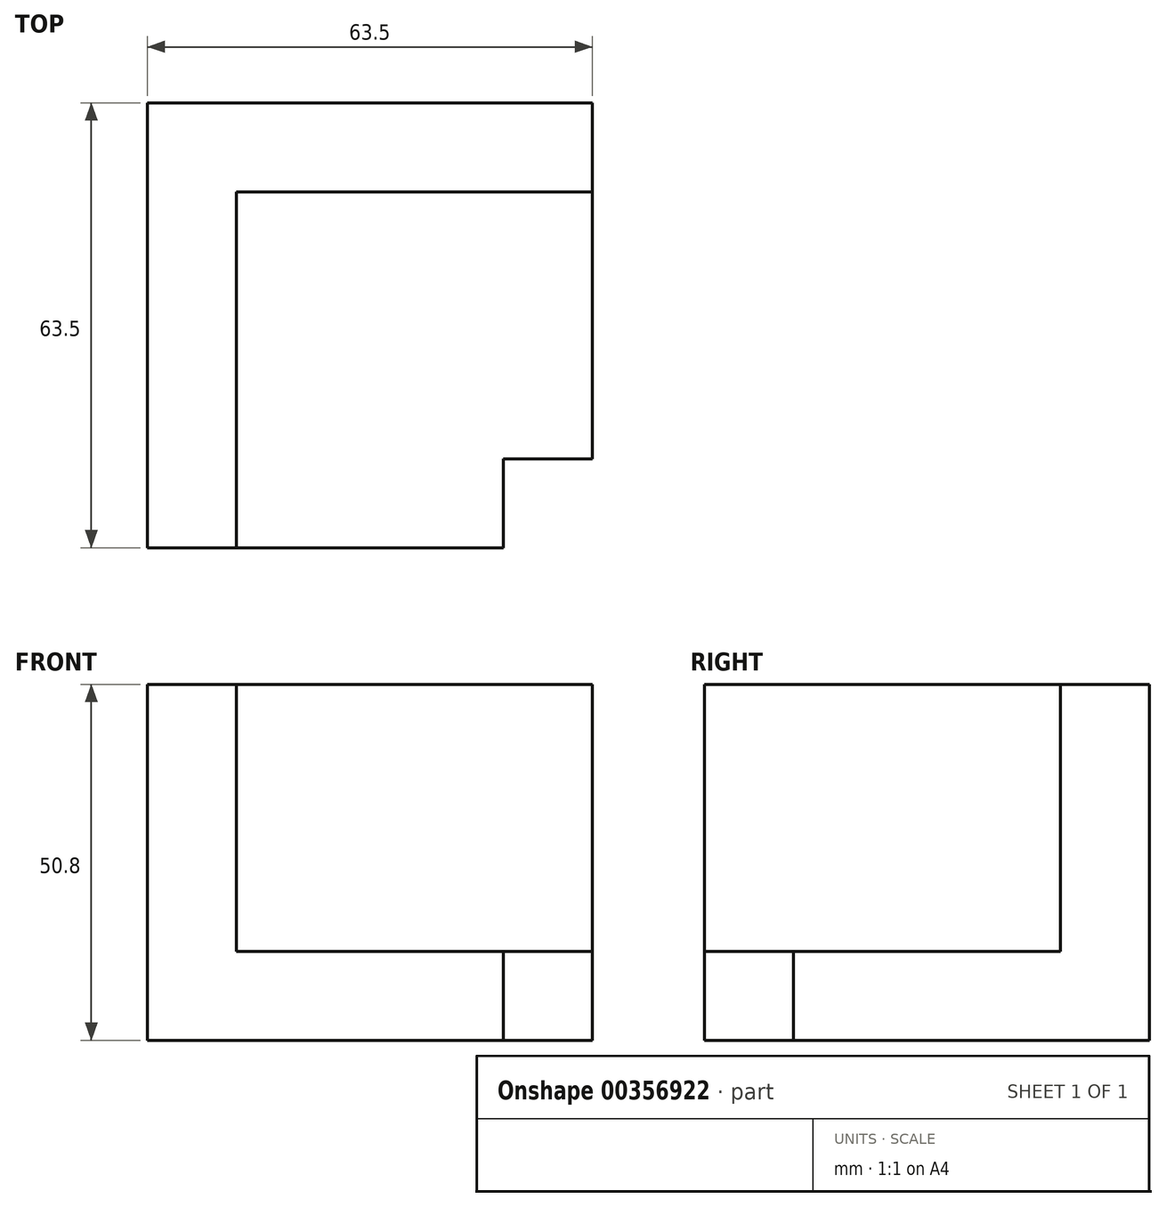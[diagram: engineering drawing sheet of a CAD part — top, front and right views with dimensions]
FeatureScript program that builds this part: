
annotation { "Feature Type Name" : "Feature", "Feature Type Description" : "" }
export const myFeature = defineFeature(function(context is Context, id is Id, definition is map)
    precondition{}
    {
        {
            var Q0;
            Q0=qCreatedBy(makeId("Front.planeOp"),FACE);
            var sketch = newSketch(context, id + "F0", { "sketchPlane" : qUnion([Q0])});
            skLineSegment(sketch, "E0.bottom", {"start": v(0, 0) * mm, "end": v(12.7, 0) * mm});
            skLineSegment(sketch, "E0.top", {"start": v(0, -50.8) * mm, "end": v(12.7, -50.8) * mm});
            skLineSegment(sketch, "E0.left", {"start": v(0, 0) * mm, "end": v(0, -50.8) * mm});
            skLineSegment(sketch, "E0.right", {"start": v(12.7, 0) * mm, "end": v(12.7, -50.8) * mm});
            skSolve(sketch);
        }
        {
            var Q0;
            Q0 = qSketchRegion(id + "F0", true);
            var Q1;
            Q1=makeQuery(id+"F0.imprint","IMPRINT",FACE,{"disambiguationData":[TD([[makeQuery(id+"F0.imprint","IMPRINT",EDGE,{"derivedFrom":sQuery(id+"F0.wireOp",EDGE,"E0.bottom")}),-1.0]])]});
            extrude(context, id + "F1", {"entities" : qUnion([Q0, Q1]), "depth" : 63.5 * mm});
        }
        {
            var Q0;
            Q0=makeQuery(id+"F1.opExtrude","SWEPT_FACE",FACE,{"disambiguationData":[OSD([sQuery(id+"F0.wireOp",EDGE,"E0.right")])]});
            var sketch = newSketch(context, id + "F2", { "sketchPlane" : qUnion([Q0])});
            skLineSegment(sketch, "E1.bottom", {"start": v(0, 0) * mm, "end": v(-12.7, 0) * mm});
            skLineSegment(sketch, "E1.top", {"start": v(0, -50.8) * mm, "end": v(-12.7, -50.8) * mm});
            skLineSegment(sketch, "E1.left", {"start": v(0, 0) * mm, "end": v(0, -50.8) * mm});
            skLineSegment(sketch, "E1.right", {"start": v(-12.7, 0) * mm, "end": v(-12.7, -50.8) * mm});
            skSolve(sketch);
        }
        {
            var Q0;
            Q0 = qSketchRegion(id + "F2", true);
            extrude(context, id + "F3", {"entities" : qUnion([Q0]), "operationType" : NewBodyOperationType.ADD, "depth" : 50.8 * mm});
        }
        {
            var Q0;
            Q0=makeQuery(id+"F1.opExtrude","SWEPT_FACE",FACE,{"disambiguationData":[OSD([sQuery(id+"F0.wireOp",EDGE,"E0.right")])]});
            var sketch = newSketch(context, id + "F4", { "sketchPlane" : qUnion([Q0])});
            skLineSegment(sketch, "E2.bottom", {"start": v(-63.5, -50.8) * mm, "end": v(-12.7, -50.8) * mm});
            skLineSegment(sketch, "E2.top", {"start": v(-63.5, -38.1) * mm, "end": v(-12.7, -38.1) * mm});
            skLineSegment(sketch, "E2.left", {"start": v(-63.5, -50.8) * mm, "end": v(-63.5, -38.1) * mm});
            skLineSegment(sketch, "E2.right", {"start": v(-12.7, -50.8) * mm, "end": v(-12.7, -38.1) * mm});
            skSolve(sketch);
        }
        {
            var Q0;
            Q0 = qSketchRegion(id + "F4", true);
            extrude(context, id + "F5", {"entities" : qUnion([Q0]), "operationType" : NewBodyOperationType.ADD, "depth" : 50.8 * mm});
        }
        {
            var Q0;
            Q0=makeQuery(id+"F5.boolean.opBoolean","MERGE",FACE,{"derivedFrom":[makeQuery(id+"F1.opExtrude","CAP_FACE",FACE,{"disambiguationData":[OSD([sQuery(id+"F0.wireOp",EDGE,"E0.bottom"),sQuery(id+"F0.wireOp",EDGE,"E0.top"),sQuery(id+"F0.wireOp",EDGE,"E0.left"),sQuery(id+"F0.wireOp",EDGE,"E0.right")])],"isStart":false}),makeQuery(id+"F5.opExtrude","SWEPT_FACE",FACE,{"disambiguationData":[OSD([sQuery(id+"F4.wireOp",EDGE,"E2.left")])]})]});
            var sketch = newSketch(context, id + "F6", { "sketchPlane" : qUnion([Q0])});
            skLineSegment(sketch, "E3.bottom", {"start": v(63.5, -38.1) * mm, "end": v(50.8, -38.1) * mm});
            skLineSegment(sketch, "E3.top", {"start": v(63.5, -50.8) * mm, "end": v(50.8, -50.8) * mm});
            skLineSegment(sketch, "E3.left", {"start": v(63.5, -38.1) * mm, "end": v(63.5, -50.8) * mm});
            skLineSegment(sketch, "E3.right", {"start": v(50.8, -38.1) * mm, "end": v(50.8, -50.8) * mm});
            skSolve(sketch);
        }
        {
            var Q0;
            Q0=makeQuery(id+"F6.imprint","IMPRINT",FACE,{"disambiguationData":[TD([[makeQuery(id+"F6.imprint","IMPRINT",EDGE,{"derivedFrom":sQuery(id+"F6.wireOp",EDGE,"E3.bottom")}),1.0]])]});
            extrude(context, id + "F7", {"entities" : qUnion([Q0]), "operationType" : NewBodyOperationType.REMOVE, "oppositeDirection" : true, "depth" : 12.7 * mm});
        }
    });
